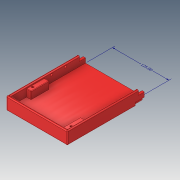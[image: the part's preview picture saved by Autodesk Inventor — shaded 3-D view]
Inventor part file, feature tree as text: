
AUTODESK INVENTOR PART (.ipt)
format: ipt  version: 2019 (Build 230136000, 136)  size: 283,136 bytes
history: native  units: mm
features: sketch x10, extrude x9, projected_geometry x3, other x2, fillet x2, plane x1
ambient origin geometry x8: Origin, YZ Plane, XZ Plane, XY Plane, X Axis, Y Axis, Z Axis, Center Point
bodies: Solid1 (feature_tree)
feature tree (27):
  other  "Annotations"
  extrude  "Extrusion1"  Depth=150.0mm
  extrude  "Extrusion2"  Depth=5.0mm
  extrude  "Extrusion3"  Depth=20.0mm TaperAngle=0.0deg
  extrude  "Extrusion4"  Depth=3.0mm
  fillet  "Fillet1"  Radius=20.0mm
  sketch  "Sketch11"  dims[d23=20.0mm d24=0.0mm d25=2.0mm]
  sketch  "Sketch12"  dims[d37=2.5mm d38=0.0mm d39=35.0mm d40=0.0mm]
  extrude  "Extrusion8"  Depth=2.0mm
  extrude  "Extrusion9"  Depth=35.0mm
  fillet  "Fillet4"  [1 undecoded]
  extrude  "Extrusion10"  Depth=40.0mm
  extrude  "Extrusion11"  TaperAngle=0.0deg  [1 undecoded]
  plane  "Work Plane3"
  extrude  "Extrusion13"  Depth=11.0mm
  sketch  "Sketch1"  dims[d0=135.0mm d1=150.0mm]
  sketch  "Sketch3"  dims[d2=8.0mm d3=0.0mm d4=5.0mm]
  projected_geometry  "Projected Loop2"
  sketch  "Sketch4"  dims[d5=5.0mm d6=20.0mm d7=0.0mm]
  projected_geometry  "Projected Loop3"
  sketch  "Sketch6"  dims[d8=3.0mm d9=3.0mm d10=20.0mm d11=0.0mm]
  sketch  "Sketch15"  dims[d41=10.0mm d42=40.0mm]
  projected_geometry  "Projected Loop7"
  sketch  "Sketch16"  dims[d43=0.0mm d44=0.0mm]
  sketch  "Sketch17"  dims[d45=40.0mm d46=11.0mm]
  sketch  "Sketch21"  dims[d47=16.0mm d48=0.0mm d49=1.0mm d50=4.5mm d51=3.5mm d52=9.0mm d53=4.5mm d54=6.0mm d56=12.0mm d57=0.0mm d60=4.5mm d61=4.5mm d62=30.8mm d64=5.0mm d65=0.0mm d66=0.0mm d67=90.0mm d76=-1.5mm d78=7.5mm d79=7.5mm d80=3.15mm d81=0.0mm d83=10.0mm d85=10.0mm d86=0.0mm d87=13.0mm d88=0.0mm d89=0.0mm d90=12.5mm d73=4.870635mm d74=1.41766mm d75=125.0mm]
  other  "Linear Dimension 1"
note: 2 required parameter values undecoded (feature->parameter linkage not recoverable at this tier; creation-order binding heuristic only, values carry confidence <= 0.55)
